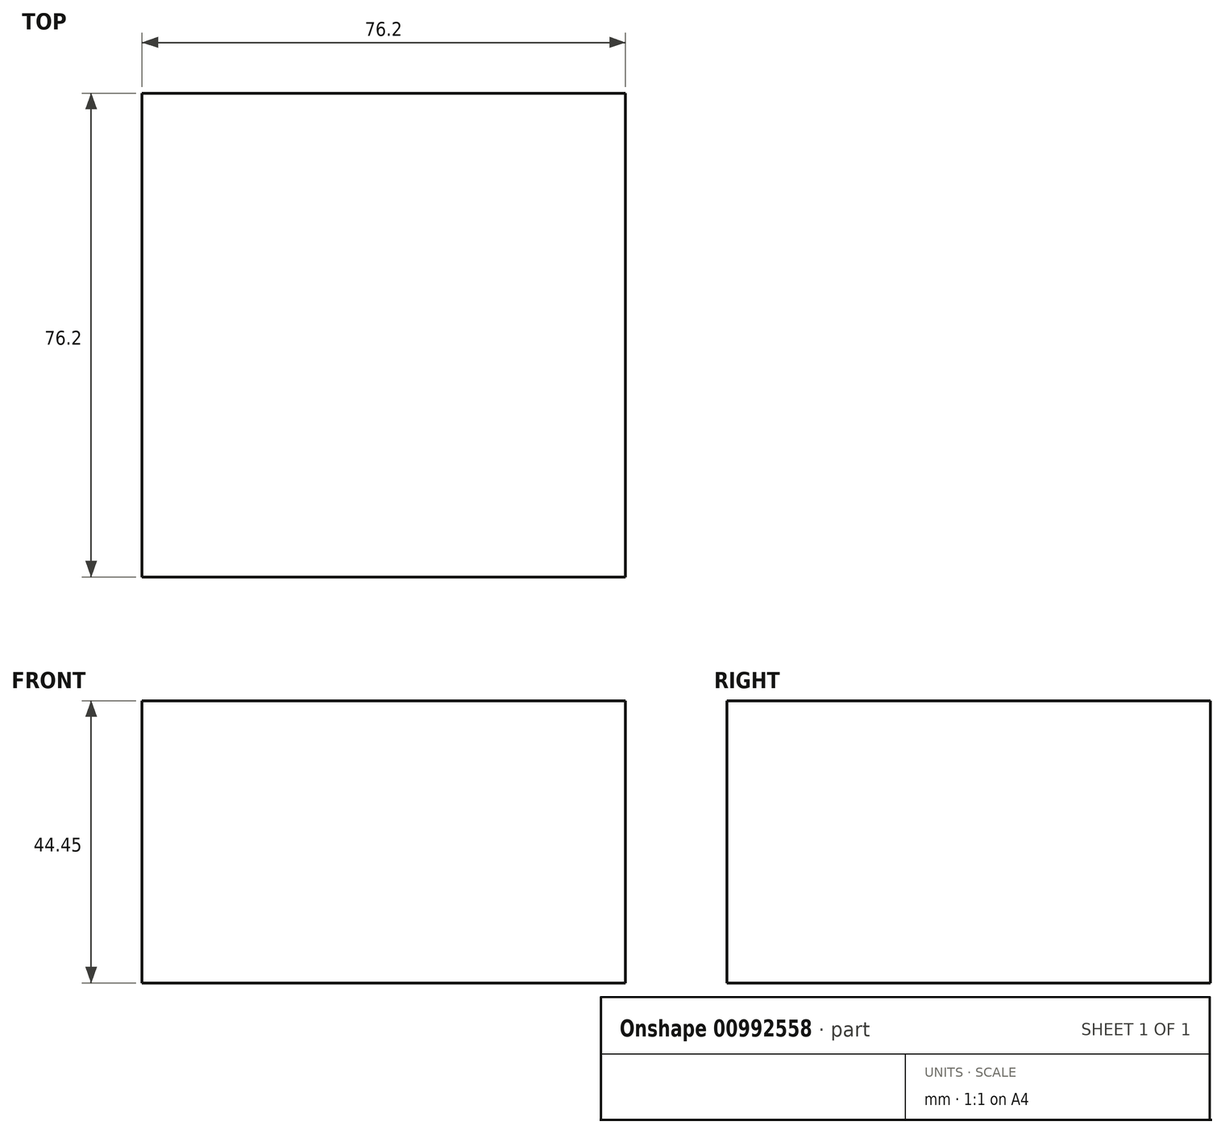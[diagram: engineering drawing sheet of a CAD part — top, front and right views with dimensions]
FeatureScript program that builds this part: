
annotation { "Feature Type Name" : "Feature", "Feature Type Description" : "" }
export const myFeature = defineFeature(function(context is Context, id is Id, definition is map)
    precondition{}
    {
        {
            var Q0;
            Q0=qCreatedBy(makeId("Front.planeOp"),FACE);
            var sketch = newSketch(context, id + "F0", { "sketchPlane" : qUnion([Q0])});
            skLineSegment(sketch, "E0.bottom", {"start": v(-39.01, 25.4) * mm, "end": v(37.19, 25.4) * mm});
            skLineSegment(sketch, "E0.top", {"start": v(-39.01, -19.05) * mm, "end": v(37.19, -19.05) * mm});
            skLineSegment(sketch, "E0.left", {"start": v(-39.01, 25.4) * mm, "end": v(-39.01, -19.05) * mm});
            skLineSegment(sketch, "E0.right", {"start": v(37.19, 25.4) * mm, "end": v(37.19, -19.05) * mm});
            skSolve(sketch);
        }
        {
            var Q0;
            Q0=qSketchRegion(id+"F0",true);
            extrude(context, id + "F1", {"entities" : qUnion([Q0]), "depth" : 76.2 * mm});
        }
    });
